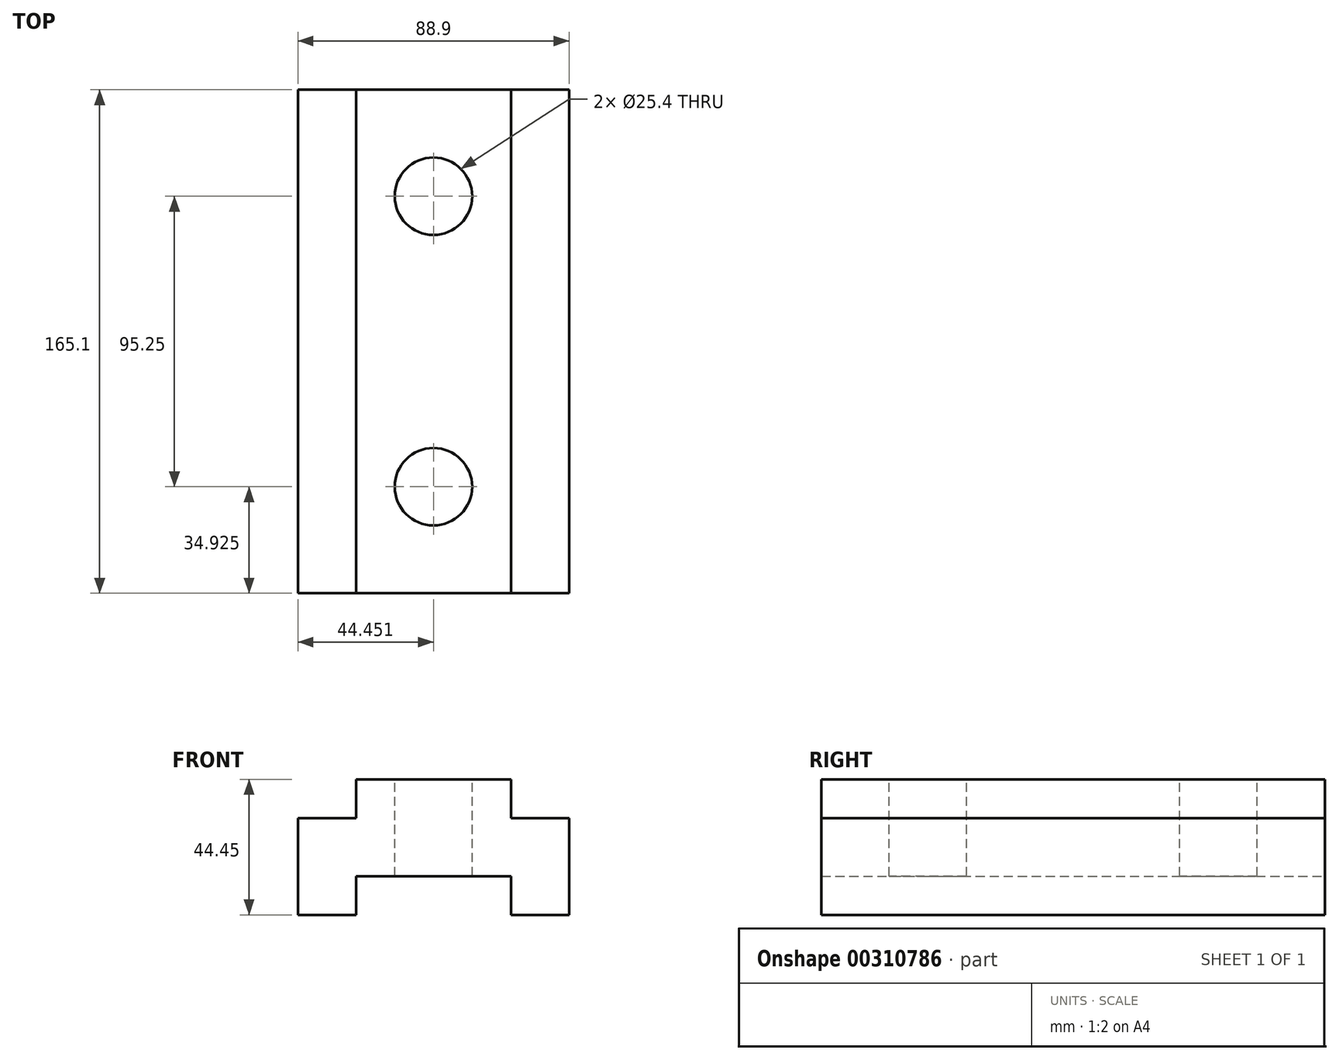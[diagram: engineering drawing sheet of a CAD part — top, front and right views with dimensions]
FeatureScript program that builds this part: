
annotation { "Feature Type Name" : "Feature", "Feature Type Description" : "" }
export const myFeature = defineFeature(function(context is Context, id is Id, definition is map)
    precondition{}
    {
        {
            var Q0;
            Q0=qCreatedBy(makeId("Front.planeOp"),FACE);
            var sketch = newSketch(context, id + "F0", { "sketchPlane" : qUnion([Q0])});
            skLineSegment(sketch, "E0", {"start": v(-52.73, -2.86) * mm, "end": v(-33.68, -2.86) * mm});
            skLineSegment(sketch, "E1", {"start": v(-52.73, 28.9) * mm, "end": v(-52.73, -2.86) * mm});
            skLineSegment(sketch, "E2", {"start": v(-52.73, 28.9) * mm, "end": v(-33.68, 28.9) * mm});
            skLineSegment(sketch, "E3", {"start": v(-33.68, -2.86) * mm, "end": v(-33.68, 9.84) * mm});
            skLineSegment(sketch, "E4", {"start": v(-33.68, 9.84) * mm, "end": v(17.12, 9.84) * mm});
            skLineSegment(sketch, "E5", {"start": v(17.12, 9.84) * mm, "end": v(17.12, -2.86) * mm});
            skLineSegment(sketch, "E6", {"start": v(17.12, -2.86) * mm, "end": v(36.17, -2.86) * mm});
            skLineSegment(sketch, "E7", {"start": v(36.17, -2.86) * mm, "end": v(36.17, 28.9) * mm});
            skLineSegment(sketch, "E8", {"start": v(36.17, 28.9) * mm, "end": v(17.12, 28.9) * mm});
            skLineSegment(sketch, "E9", {"start": v(17.12, 28.9) * mm, "end": v(17.12, 41.6) * mm});
            skLineSegment(sketch, "E10", {"start": v(17.12, 41.6) * mm, "end": v(-33.68, 41.6) * mm});
            skLineSegment(sketch, "E11", {"start": v(-33.68, 41.6) * mm, "end": v(-33.68, 28.9) * mm});
            skSolve(sketch);
        }
        {
            var Q0;
            Q0=makeQuery(id+"F0.imprint","IMPRINT",FACE,{"disambiguationData":[TD([[makeQuery(id+"F0.imprint","IMPRINT",EDGE,{"derivedFrom":sQuery(id+"F0.wireOp",EDGE,"E0")}),1.0]])]});
            extrude(context, id + "F1", {"entities" : qUnion([Q0]), "depth" : 165.1 * mm});
        }
        {
            var Q0;
            Q0=makeQuery(id+"F1.opExtrude","SWEPT_FACE",FACE,{"disambiguationData":[OSD([sQuery(id+"F0.wireOp",EDGE,"E10")])]});
            var sketch = newSketch(context, id + "F2", { "sketchPlane" : qUnion([Q0])});
            skCircle(sketch, "E12", {"center": v(-8.28, -130.18) * mm, "radius": 12.7 * mm});
            skCircle(sketch, "E13", {"center": v(-8.28, -34.92) * mm, "radius": 12.7 * mm});
            skSolve(sketch);
        }
        {
            var Q0;
            Q0=makeQuery(id+"F2.imprint","IMPRINT",FACE,{"disambiguationData":[TD([[makeQuery(id+"F2.imprint","IMPRINT",EDGE,{"derivedFrom":sQuery(id+"F2.wireOp",EDGE,"E12")}),1.0]])]});
            var Q1;
            Q1=makeQuery(id+"F2.imprint","IMPRINT",FACE,{"disambiguationData":[TD([[makeQuery(id+"F2.imprint","IMPRINT",EDGE,{"derivedFrom":sQuery(id+"F2.wireOp",EDGE,"E13")}),1.0]])]});
            extrude(context, id + "F3", {"entities" : qUnion([Q0, Q1]), "operationType" : NewBodyOperationType.REMOVE, "oppositeDirection" : true, "depth" : 50.8 * mm});
        }
    });
